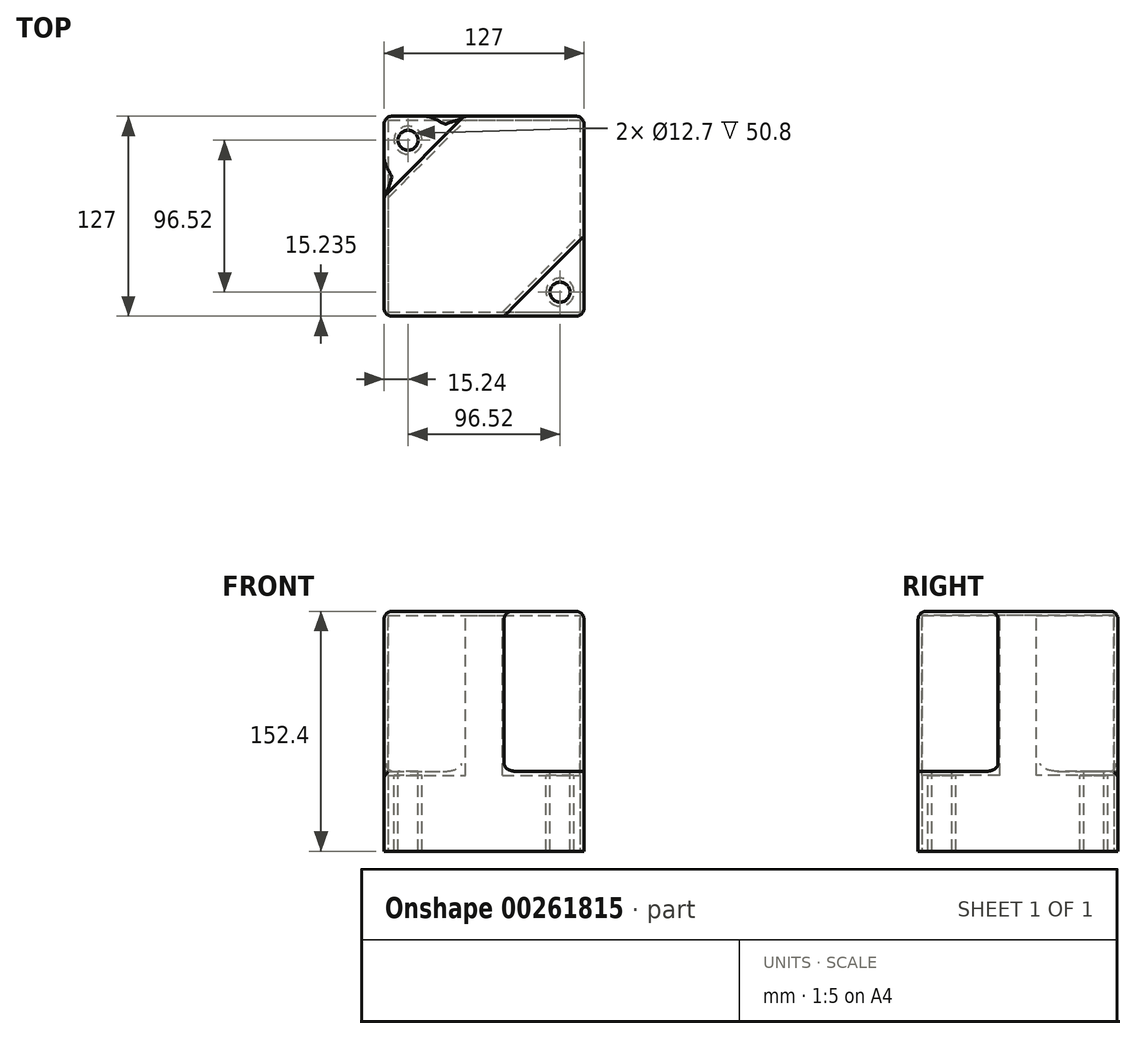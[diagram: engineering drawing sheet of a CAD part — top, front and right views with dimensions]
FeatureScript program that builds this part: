
annotation { "Feature Type Name" : "Feature", "Feature Type Description" : "" }
export const myFeature = defineFeature(function(context is Context, id is Id, definition is map)
    precondition{}
    {
        {
            var Q0;
            Q0=qCreatedBy(makeId("Top.planeOp"),FACE);
            var sketch = newSketch(context, id + "F0", { "sketchPlane" : qUnion([Q0])});
            skLineSegment(sketch, "E0.bottom", {"start": v(-59.67, 57.64) * mm, "end": v(67.33, 57.64) * mm});
            skLineSegment(sketch, "E0.top", {"start": v(-59.67, -69.36) * mm, "end": v(67.33, -69.36) * mm});
            skLineSegment(sketch, "E0.left", {"start": v(-59.67, 57.64) * mm, "end": v(-59.67, -69.36) * mm});
            skLineSegment(sketch, "E0.right", {"start": v(67.33, 57.64) * mm, "end": v(67.33, -69.36) * mm});
            skSolve(sketch);
        }
        {
            var Q0;
            Q0=makeQuery(id+"F0.imprint","IMPRINT",FACE,{"disambiguationData":[TD([[makeQuery(id+"F0.imprint","IMPRINT",EDGE,{"derivedFrom":sQuery(id+"F0.wireOp",EDGE,"E0.bottom")}),-1.0]])]});
            extrude(context, id + "F1", {"entities" : qUnion([Q0]), "depth" : 152.4 * mm});
        }
        {
            var Q0;
            Q0=makeQuery(id+"F1.opExtrude","CAP_FACE",FACE,{"disambiguationData":[OSD([sQuery(id+"F0.wireOp",EDGE,"E0.bottom"),sQuery(id+"F0.wireOp",EDGE,"E0.top"),sQuery(id+"F0.wireOp",EDGE,"E0.left"),sQuery(id+"F0.wireOp",EDGE,"E0.right")])],"isStart":false});
            var sketch = newSketch(context, id + "F2", { "sketchPlane" : qUnion([Q0])});
            skLineSegment(sketch, "E1", {"start": v(-59.67, 57.64) * mm, "end": v(-8.87, 57.64) * mm});
            skLineSegment(sketch, "E2", {"start": v(-59.67, 57.64) * mm, "end": v(-59.67, 6.84) * mm});
            skLineSegment(sketch, "E3", {"start": v(67.33, -69.36) * mm, "end": v(16.53, -69.36) * mm});
            skLineSegment(sketch, "E4", {"start": v(67.33, -69.36) * mm, "end": v(67.33, -18.56) * mm});
            skLineSegment(sketch, "E5", {"start": v(-59.67, 6.84) * mm, "end": v(-8.87, 57.64) * mm});
            skLineSegment(sketch, "E6", {"start": v(16.53, -69.36) * mm, "end": v(67.33, -18.56) * mm});
            skSolve(sketch);
        }
        {
            var Q0;
            Q0=makeQuery(id+"F2.imprint","IMPRINT",FACE,{"disambiguationData":[TD([[makeQuery(id+"F2.imprint","IMPRINT",EDGE,{"derivedFrom":sQuery(id+"F2.wireOp",EDGE,"E1")}),-1.0]])]});
            var Q1;
            Q1=makeQuery(id+"F2.imprint","IMPRINT",FACE,{"disambiguationData":[TD([[makeQuery(id+"F2.imprint","IMPRINT",EDGE,{"derivedFrom":sQuery(id+"F2.wireOp",EDGE,"E3")}),1.0]])]});
            extrude(context, id + "F3", {"entities" : qUnion([Q0, Q1]), "operationType" : NewBodyOperationType.REMOVE, "oppositeDirection" : true, "depth" : 101.6 * mm});
        }
        {
            var Q0;
            Q0=makeQuery(id+"F3.boolean.opBoolean","COPY",FACE,{"derivedFrom":makeQuery(id+"F3.opExtrude","CAP_FACE",FACE,{"disambiguationData":[OSD([sQuery(id+"F2.wireOp",EDGE,"E1"),sQuery(id+"F2.wireOp",EDGE,"E2"),sQuery(id+"F2.wireOp",EDGE,"E5")])],"isStart":false})});
            var sketch = newSketch(context, id + "F4", { "sketchPlane" : qUnion([Q0])});
            skCircle(sketch, "E7", {"center": v(-44.43, 42.4) * mm, "radius": 6.35 * mm});
            skCircle(sketch, "E8", {"center": v(52.09, -54.12) * mm, "radius": 6.35 * mm});
            skSolve(sketch);
        }
        {
            var Q0;
            Q0=makeQuery(id+"F4.imprint","IMPRINT",FACE,{"disambiguationData":[TD([[makeQuery(id+"F4.imprint","IMPRINT",EDGE,{"derivedFrom":sQuery(id+"F4.wireOp",EDGE,"E7")}),1.0]])]});
            var Q1;
            Q1=makeQuery(id+"F4.imprint","IMPRINT",FACE,{"disambiguationData":[TD([[makeQuery(id+"F4.imprint","IMPRINT",EDGE,{"derivedFrom":sQuery(id+"F4.wireOp",EDGE,"E8")}),1.0]])]});
            extrude(context, id + "F5", {"entities" : qUnion([Q0, Q1]), "operationType" : NewBodyOperationType.REMOVE, "oppositeDirection" : true, "depth" : 203.2 * mm});
        }
        {
            var Q0;
            Q0=makeQuery(id+"F1.opExtrude","CAP_FACE",FACE,{"disambiguationData":[OSD([sQuery(id+"F0.wireOp",EDGE,"E0.bottom"),sQuery(id+"F0.wireOp",EDGE,"E0.top"),sQuery(id+"F0.wireOp",EDGE,"E0.left"),sQuery(id+"F0.wireOp",EDGE,"E0.right")])],"isStart":true});
            shell(context, id + "F6", {"entities" : qUnion([Q0]), "thickness" : 2.54 * mm});
        }
        {
            var Q0;
            Q0=makeQuery(id+"F1.opExtrude","SWEPT_EDGE",EDGE,{"disambiguationData":[OSD([sQuery(id+"F0.wireOp",EDGE,"E0.top"),sQuery(id+"F0.wireOp",EDGE,"E0.left")])]});
            var Q1;
            Q1=makeQuery(id+"F3.boolean.opBoolean","COPY",EDGE,{"derivedFrom":makeQuery(id+"F3.opExtrude","SWEPT_EDGE",EDGE,{"disambiguationData":[OSD([sQuery(id+"F0.wireOp",EDGE,"E0.top"),sQuery(id+"F2.wireOp",EDGE,"E3"),sQuery(id+"F2.wireOp",EDGE,"E6")])]})});
            var Q2;
            Q2=makeQuery(id+"F1.opExtrude","CAP_EDGE",EDGE,{"disambiguationData":[OSD([sQuery(id+"F0.wireOp",EDGE,"E0.top")])],"isStart":false});
            var Q3;
            Q3=makeQuery(id+"F3.boolean.opBoolean","COPY",EDGE,{"derivedFrom":makeQuery(id+"F3.opExtrude","CAP_EDGE",EDGE,{"disambiguationData":[OSD([sQuery(id+"F2.wireOp",EDGE,"E3")])],"isStart":false})});
            var Q4;
            Q4=makeQuery(id+"F1.opExtrude","SWEPT_EDGE",EDGE,{"disambiguationData":[OSD([sQuery(id+"F0.wireOp",EDGE,"E0.top"),sQuery(id+"F0.wireOp",EDGE,"E0.right")])]});
            var Q5;
            Q5=makeQuery(id+"F3.boolean.opBoolean","COPY",EDGE,{"derivedFrom":makeQuery(id+"F3.opExtrude","CAP_EDGE",EDGE,{"disambiguationData":[OSD([sQuery(id+"F2.wireOp",EDGE,"E4")])],"isStart":false})});
            var Q6;
            Q6=makeQuery(id+"F3.boolean.opBoolean","COPY",EDGE,{"derivedFrom":makeQuery(id+"F3.opExtrude","CAP_EDGE",EDGE,{"disambiguationData":[OSD([sQuery(id+"F2.wireOp",EDGE,"E1")])],"isStart":false})});
            var Q7;
            Q7=makeQuery(id+"F3.boolean.opBoolean","COPY",EDGE,{"derivedFrom":makeQuery(id+"F3.opExtrude","SWEPT_EDGE",EDGE,{"disambiguationData":[OSD([sQuery(id+"F0.wireOp",EDGE,"E0.bottom"),sQuery(id+"F2.wireOp",EDGE,"E1"),sQuery(id+"F2.wireOp",EDGE,"E5")])]})});
            var Q8;
            Q8=makeQuery(id+"F1.opExtrude","CAP_EDGE",EDGE,{"disambiguationData":[OSD([sQuery(id+"F0.wireOp",EDGE,"E0.bottom")])],"isStart":false});
            var Q9;
            Q9=makeQuery(id+"F3.boolean.opBoolean","COPY",EDGE,{"derivedFrom":makeQuery(id+"F3.opExtrude","CAP_EDGE",EDGE,{"disambiguationData":[OSD([sQuery(id+"F2.wireOp",EDGE,"E5")])],"isStart":true})});
            var Q10;
            Q10=makeQuery(id+"F3.boolean.opBoolean","COPY",EDGE,{"derivedFrom":makeQuery(id+"F3.opExtrude","CAP_EDGE",EDGE,{"disambiguationData":[OSD([sQuery(id+"F2.wireOp",EDGE,"E5")])],"isStart":false})});
            var Q11;
            Q11=makeQuery(id+"F3.boolean.opBoolean","COPY",EDGE,{"derivedFrom":makeQuery(id+"F3.opExtrude","CAP_EDGE",EDGE,{"disambiguationData":[OSD([sQuery(id+"F2.wireOp",EDGE,"E2")])],"isStart":false})});
            var Q12;
            Q12=makeQuery(id+"F3.boolean.opBoolean","COPY",FACE,{"derivedFrom":makeQuery(id+"F3.opExtrude","SWEPT_FACE",FACE,{"disambiguationData":[OSD([sQuery(id+"F2.wireOp",EDGE,"E5")])]})});
            var Q13;
            Q13=makeQuery(id+"F1.opExtrude","CAP_EDGE",EDGE,{"disambiguationData":[OSD([sQuery(id+"F0.wireOp",EDGE,"E0.left")])],"isStart":false});
            var Q14;
            Q14=makeQuery(id+"F1.opExtrude","SWEPT_EDGE",EDGE,{"disambiguationData":[OSD([sQuery(id+"F0.wireOp",EDGE,"E0.bottom"),sQuery(id+"F0.wireOp",EDGE,"E0.left")])]});
            var Q15;
            Q15=makeQuery(id+"F3.boolean.opBoolean","COPY",EDGE,{"derivedFrom":makeQuery(id+"F3.opExtrude","CAP_EDGE",EDGE,{"disambiguationData":[OSD([sQuery(id+"F2.wireOp",EDGE,"E6")])],"isStart":true})});
            var Q16;
            Q16=makeQuery(id+"F1.opExtrude","CAP_EDGE",EDGE,{"disambiguationData":[OSD([sQuery(id+"F0.wireOp",EDGE,"E0.right")])],"isStart":false});
            var Q17;
            Q17=makeQuery(id+"F1.opExtrude","SWEPT_EDGE",EDGE,{"disambiguationData":[OSD([sQuery(id+"F0.wireOp",EDGE,"E0.bottom"),sQuery(id+"F0.wireOp",EDGE,"E0.right")])]});
            var Q18;
            Q18=makeQuery(id+"F3.boolean.opBoolean","COPY",EDGE,{"derivedFrom":makeQuery(id+"F3.opExtrude","SWEPT_EDGE",EDGE,{"disambiguationData":[OSD([sQuery(id+"F0.wireOp",EDGE,"E0.right"),sQuery(id+"F2.wireOp",EDGE,"E4"),sQuery(id+"F2.wireOp",EDGE,"E6")])]})});
            var Q19;
            Q19=makeQuery(id+"F3.boolean.opBoolean","COPY",EDGE,{"derivedFrom":makeQuery(id+"F3.opExtrude","CAP_EDGE",EDGE,{"disambiguationData":[OSD([sQuery(id+"F2.wireOp",EDGE,"E6")])],"isStart":false})});
            fillet(context, id + "F7", {"entities" : qUnion([Q0, Q1, Q2, Q3, Q4, Q5, Q6, Q7, Q8, Q9, Q10, Q11, Q12, Q13, Q14, Q15, Q16, Q17, Q18, Q19]), "radius" : 5.08 * mm, "tangentPropagation" : true, "allowEdgeOverflow" : false});
        }
    });
